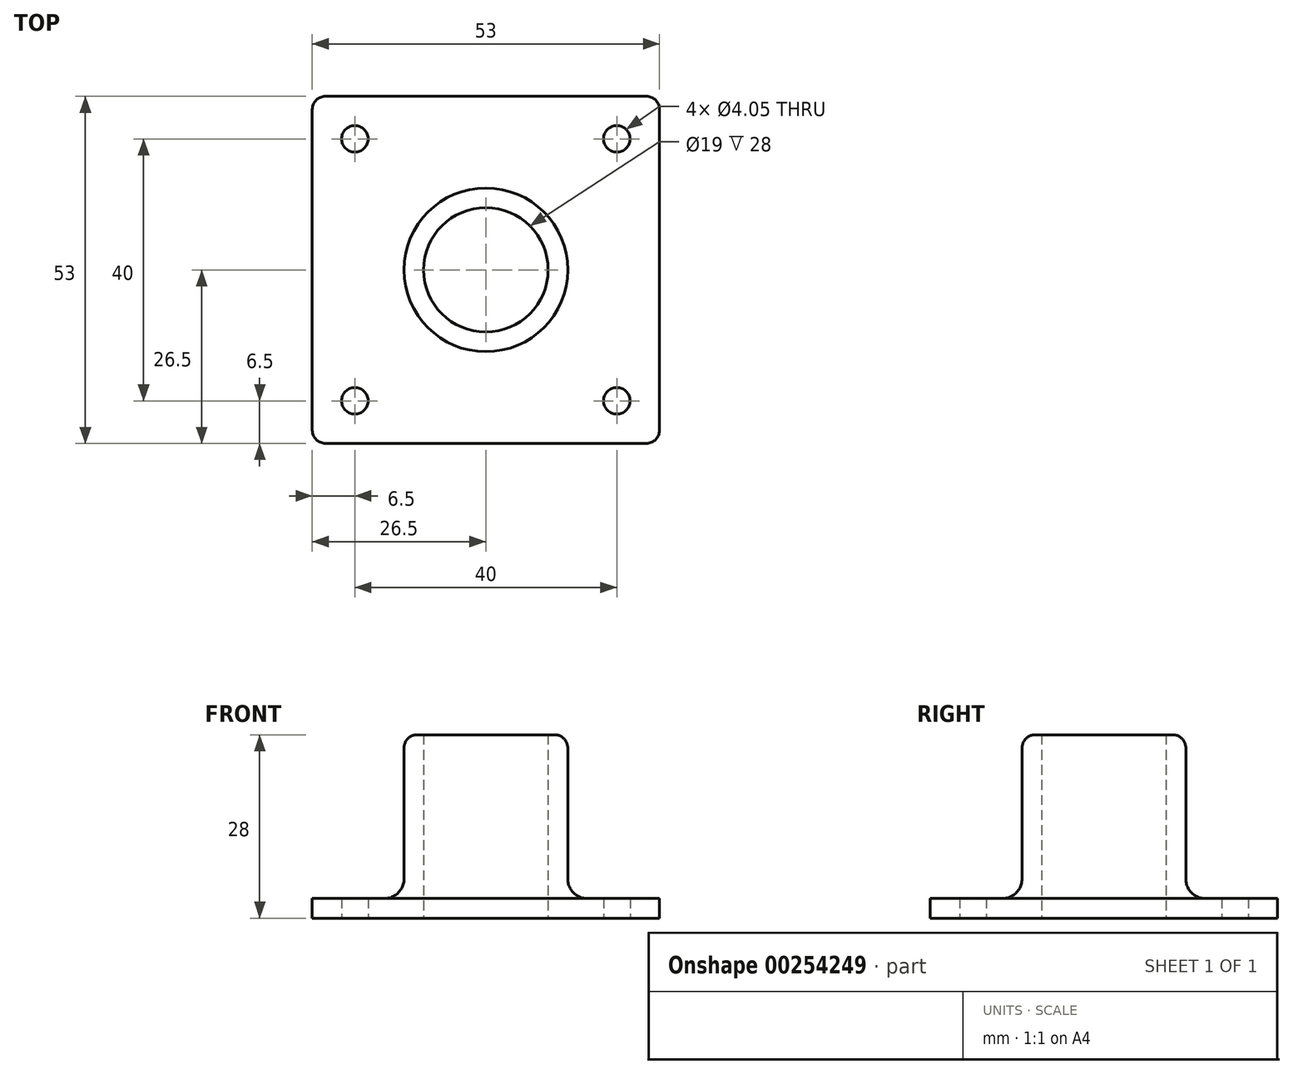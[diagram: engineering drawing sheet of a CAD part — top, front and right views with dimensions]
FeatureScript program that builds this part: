
annotation { "Feature Type Name" : "Feature", "Feature Type Description" : "" }
export const myFeature = defineFeature(function(context is Context, id is Id, definition is map)
    precondition{}
    {
        {
            var Q0;
            Q0=qCreatedBy(makeId("Top.planeOp"),FACE);
            var sketch = newSketch(context, id + "F0", { "sketchPlane" : qUnion([Q0])});
            skLineSegment(sketch, "E0.bottom", {"start": v(26.5, 26.5) * mm, "end": v(-26.5, 26.5) * mm});
            skLineSegment(sketch, "E0.top", {"start": v(26.5, -26.5) * mm, "end": v(-26.5, -26.5) * mm});
            skLineSegment(sketch, "E0.left", {"start": v(26.5, 26.5) * mm, "end": v(26.5, -26.5) * mm});
            skLineSegment(sketch, "E0.right", {"start": v(-26.5, 26.5) * mm, "end": v(-26.5, -26.5) * mm});
            skPoint(sketch, "E0.middle", {"position": v(0, 0) * mm});
            skCircle(sketch, "E1", {"center": v(0, 0) * mm, "radius": 9.5 * mm});
            skCircle(sketch, "E2", {"center": v(0, 0) * mm, "radius": 12.5 * mm});
            skCircle(sketch, "E3", {"center": v(-20, 20) * mm, "radius": 2.02 * mm});
            skCircle(sketch, "E4", {"center": v(20, 20) * mm, "radius": 2.02 * mm});
            skCircle(sketch, "E5", {"center": v(-20, -20) * mm, "radius": 2.02 * mm});
            skCircle(sketch, "E6", {"center": v(20, -20) * mm, "radius": 2.02 * mm});
            skSolve(sketch);
        }
        {
            var Q0;
            Q0 = qSketchRegion(id + "F0", true);
            var Q1;
            Q1=makeQuery(id+"F0.imprint","IMPRINT",FACE,{"disambiguationData":[TD([[makeQuery(id+"F0.imprint","IMPRINT",EDGE,{"derivedFrom":sQuery(id+"F0.wireOp",EDGE,"E1")}),-1.0]])]});
            extrude(context, id + "F1", {"entities" : qUnion([Q0, Q1]), "depth" : 3 * mm});
        }
        {
            var Q0;
            Q0=makeQuery(id+"F0.imprint","IMPRINT",FACE,{"disambiguationData":[TD([[makeQuery(id+"F0.imprint","IMPRINT",EDGE,{"derivedFrom":sQuery(id+"F0.wireOp",EDGE,"E1")}),-1.0]])]});
            var Q1;
            Q1=sQuery(id+"F0.wireOp",EDGE,"E2");
            var Q2;
            Q2=sQuery(id+"F0.wireOp",EDGE,"E1");
            extrude(context, id + "F2", {"entities" : qUnion([Q0]), "operationType" : NewBodyOperationType.ADD, "surfaceEntities" : qUnion([Q1, Q2]), "depth" : 28 * mm});
        }
        {
            var Q0;
            Q0=makeQuery(id+"F2.opExtrude","CAP_EDGE",EDGE,{"disambiguationData":[OSD([sQuery(id+"F0.wireOp",EDGE,"E2")])],"isStart":false});
            fillet(context, id + "F3", {"entities" : qUnion([Q0]), "radius" : 2 * mm, "tangentPropagation" : true, "allowEdgeOverflow" : false});
        }
        {
            var Q0;
            Q0=makeQuery(id+"F2.boolean.opBoolean","INTERSECT",EDGE,{"derivedFrom":[makeQuery(id+"F1.opExtrude","CAP_FACE",FACE,{"disambiguationData":[OSD([sQuery(id+"F0.wireOp",EDGE,"E0.bottom"),sQuery(id+"F0.wireOp",EDGE,"E0.top"),sQuery(id+"F0.wireOp",EDGE,"E0.left"),sQuery(id+"F0.wireOp",EDGE,"E0.right"),sQuery(id+"F0.wireOp",EDGE,"E1"),sQuery(id+"F0.wireOp",EDGE,"E3"),sQuery(id+"F0.wireOp",EDGE,"E4"),sQuery(id+"F0.wireOp",EDGE,"E5"),sQuery(id+"F0.wireOp",EDGE,"E6")])],"isStart":false}),makeQuery(id+"F2.opExtrude","SWEPT_FACE",FACE,{"disambiguationData":[OSD([sQuery(id+"F0.wireOp",EDGE,"E2")])]})]});
            fillet(context, id + "F4", {"entities" : qUnion([Q0]), "radius" : 3 * mm, "tangentPropagation" : true, "allowEdgeOverflow" : false});
        }
        {
            var Q0;
            Q0=makeQuery(id+"F1.opExtrude","SWEPT_EDGE",EDGE,{"disambiguationData":[OSD([sQuery(id+"F0.wireOp",EDGE,"E0.top"),sQuery(id+"F0.wireOp",EDGE,"E0.right")])]});
            var Q1;
            Q1=makeQuery(id+"F1.opExtrude","SWEPT_EDGE",EDGE,{"disambiguationData":[OSD([sQuery(id+"F0.wireOp",EDGE,"E0.top"),sQuery(id+"F0.wireOp",EDGE,"E0.left")])]});
            var Q2;
            Q2=makeQuery(id+"F1.opExtrude","SWEPT_EDGE",EDGE,{"disambiguationData":[OSD([sQuery(id+"F0.wireOp",EDGE,"E0.bottom"),sQuery(id+"F0.wireOp",EDGE,"E0.left")])]});
            var Q3;
            Q3=makeQuery(id+"F1.opExtrude","SWEPT_EDGE",EDGE,{"disambiguationData":[OSD([sQuery(id+"F0.wireOp",EDGE,"E0.bottom"),sQuery(id+"F0.wireOp",EDGE,"E0.right")])]});
            fillet(context, id + "F5", {"entities" : qUnion([Q0, Q1, Q2, Q3]), "radius" : 2 * mm, "tangentPropagation" : true, "allowEdgeOverflow" : false});
        }
    });
